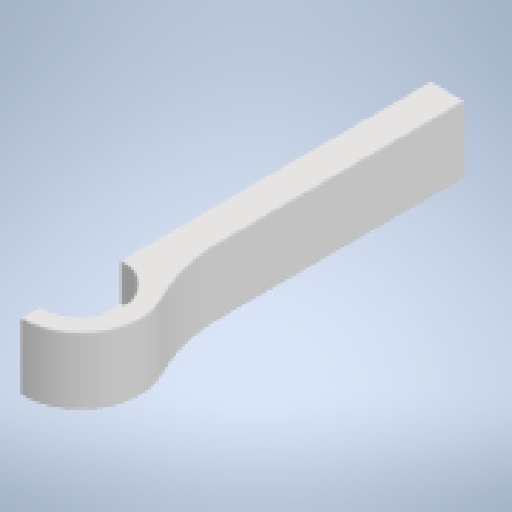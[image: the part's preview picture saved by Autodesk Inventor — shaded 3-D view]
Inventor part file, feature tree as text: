
AUTODESK INVENTOR PART (.ipt)
format: ipt  version: 2025.1 (Build 291241000, 241)  size: 305,152 bytes
history: native  units: mm
features: extrude x6, sketch x6, fillet x3
ambient origin geometry x8: Origin, YZ Plane, XZ Plane, XY Plane, X Axis, Y Axis, Z Axis, Center Point
bodies: Body1 (feature_tree)
feature tree (15):
  extrude  "Extrusion1"  TaperAngle=0.0deg  [1 undecoded]
  extrude  "Extrusion2"  Depth=10.0mm TaperAngle=0.0deg
  fillet  "Rundung1"  Radius=5.0mm
  fillet  "Rundung2"  Radius=5.0mm
  extrude  "Extrusion3"  Depth=5.6mm TaperAngle=0.0deg
  fillet  "Rundung3"  Radius=0.2mm
  extrude  "Extrusion4"  Depth=0.2mm
  extrude  "Extrusion5"  Depth=0.2mm
  extrude  "Extrusion6"  Depth=5.0mm
  sketch  "Skizze1"  dims[d1=18.0mm d4=25.0mm d7=0.0mm d8=52.5mm d9=0.0mm]
  sketch  "Skizze4"  dims[d10=0.0mm d11=10.0mm d12=0.0mm d20=5.0mm d21=5.0mm]
  sketch  "Skizze5"  dims[d22=12.1mm d23=5.6mm d24=0.0mm d25=0.2mm]
  sketch  "Skizze6"  dims[d26=0.2mm d27=3.5mm]
  sketch  "Skizze7"  dims[d28=4.2mm d29=0.0mm d30=0.2mm]
  sketch  "Skizze8"  dims[d31=3.5mm d32=5.0mm d33=5.0mm d34=4.0mm d35=0.0mm d36=8.0mm d37=3.0mm d38=0.0mm d39=10.0mm d40=0.0mm]
note: 1 required parameter value undecoded (feature->parameter linkage not recoverable at this tier; creation-order binding heuristic only, values carry confidence <= 0.55)
